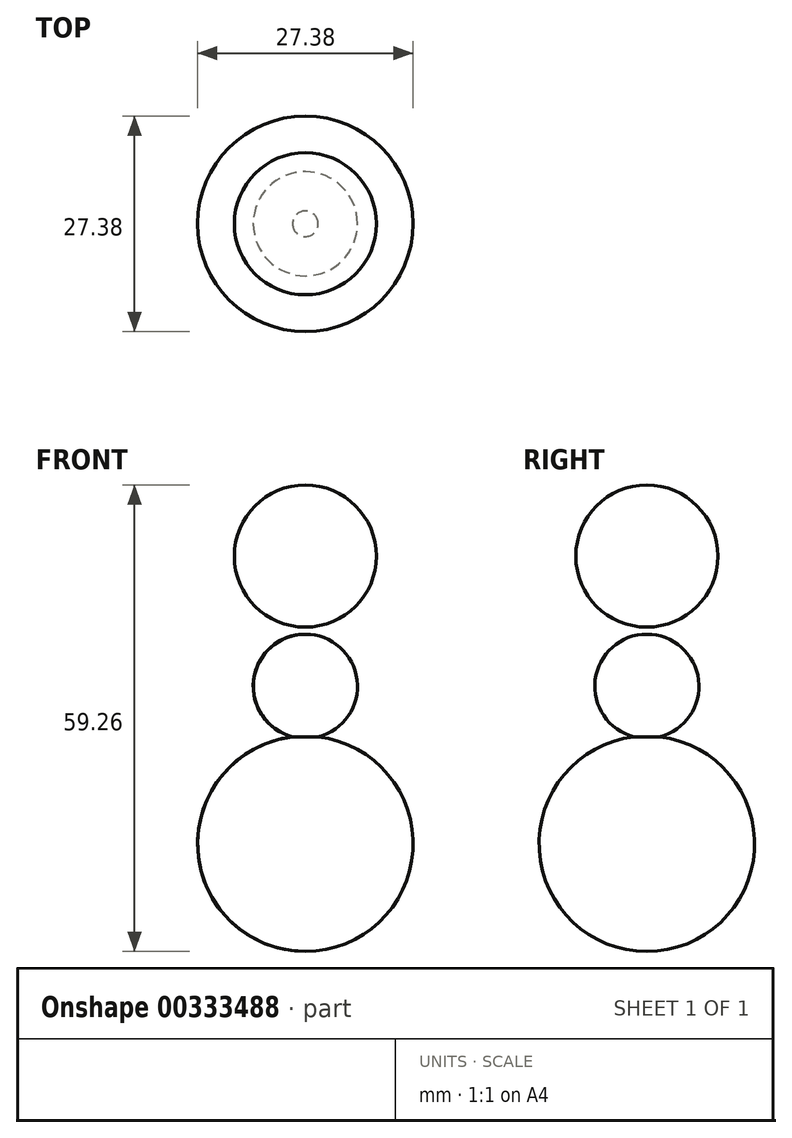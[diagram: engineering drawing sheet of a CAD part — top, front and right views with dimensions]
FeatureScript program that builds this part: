
annotation { "Feature Type Name" : "Feature", "Feature Type Description" : "" }
export const myFeature = defineFeature(function(context is Context, id is Id, definition is map)
    precondition{}
    {
        {
            var Q0;
            Q0=qCreatedBy(makeId("Front.planeOp"),FACE);
            var sketch = newSketch(context, id + "F0", { "sketchPlane" : qUnion([Q0])});
            skLineSegment(sketch, "E0", {"start": v(0, 0) * mm, "end": v(0, 27.37) * mm});
            skArc(sketch, "E1", {"start": v(0, 27.37) * mm, "mid": v(13.69, 13.69) * mm, "end": v(0, 0) * mm});
            skSolve(sketch);
        }
        {
            var Q0;
            Q0=makeQuery(id+"F0.imprint","IMPRINT",FACE,{"disambiguationData":[TD([[makeQuery(id+"F0.imprint","IMPRINT",EDGE,{"derivedFrom":sQuery(id+"F0.wireOp",EDGE,"E0")}),-1.0]])]});
            var Q1;
            Q1=sQuery(id+"F0.wireOp",EDGE,"E0");
            revolve(context, id + "F1", {"entities" : qUnion([Q0]), "axis" : qUnion([Q1]), "revolveType" : RevolveType.FULL});
        }
        {
            var Q0;
            Q0=qCreatedBy(makeId("Front.planeOp"),FACE);
            var sketch = newSketch(context, id + "F2", { "sketchPlane" : qUnion([Q0])});
            skLineSegment(sketch, "E2", {"start": v(0, 27.07) * mm, "end": v(0, 40.3) * mm});
            skArc(sketch, "E3", {"start": v(0, 40.3) * mm, "mid": v(6.62, 33.69) * mm, "end": v(0, 27.07) * mm});
            skSolve(sketch);
        }
        {
            var Q0;
            Q0=makeQuery(id+"F2.imprint","IMPRINT",FACE,{"disambiguationData":[TD([[makeQuery(id+"F2.imprint","IMPRINT",EDGE,{"derivedFrom":sQuery(id+"F2.wireOp",EDGE,"E2")}),-1.0]])]});
            var Q1;
            Q1=sQuery(id+"F2.wireOp",EDGE,"E2");
            revolve(context, id + "F3", {"operationType" : NewBodyOperationType.ADD, "entities" : qUnion([Q0]), "axis" : qUnion([Q1]), "revolveType" : RevolveType.FULL});
        }
        {
            var Q0;
            Q0=qCreatedBy(makeId("Front.planeOp"),FACE);
            var sketch = newSketch(context, id + "F4", { "sketchPlane" : qUnion([Q0])});
            skLineSegment(sketch, "E4", {"start": v(0, 41.2) * mm, "end": v(0, 59.26) * mm});
            skArc(sketch, "E5", {"start": v(0, 59.26) * mm, "mid": v(9.02, 50.23) * mm, "end": v(0, 41.2) * mm});
            skSolve(sketch);
        }
        {
            var Q0;
            Q0=makeQuery(id+"F4.imprint","IMPRINT",FACE,{"disambiguationData":[TD([[makeQuery(id+"F4.imprint","IMPRINT",EDGE,{"derivedFrom":sQuery(id+"F4.wireOp",EDGE,"E4")}),-1.0]])]});
            var Q1;
            Q1=sQuery(id+"F4.wireOp",EDGE,"E4");
            revolve(context, id + "F5", {"entities" : qUnion([Q0]), "axis" : qUnion([Q1]), "revolveType" : RevolveType.FULL});
        }
    });
